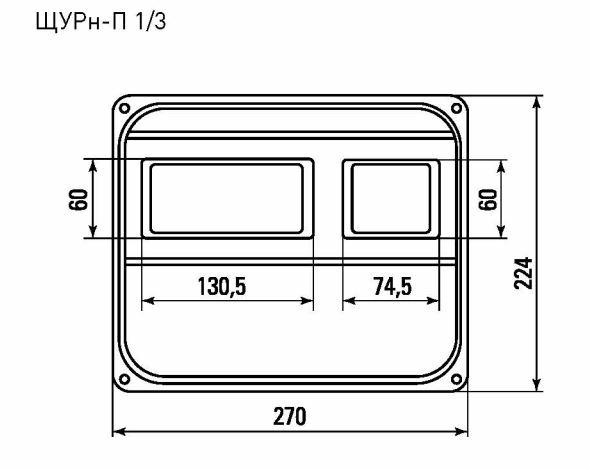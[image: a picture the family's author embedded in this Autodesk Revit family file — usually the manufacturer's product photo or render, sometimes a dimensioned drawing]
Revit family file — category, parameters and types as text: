
# Revit family: EKF_EE_ЩУР_Для_УЭРМС_(580х300х150)_IP31_Basic
name_source: partatom
category: Электрооборудование
units: mm (PartAtom-declared; Revit-internal decimal feet)

## family parameters
Всегда вертикально = Да
На основе рабочей плоскости = Нет
Общий = Нет
При загрузке вырезать с полостями = Нет
Размер круглого соединителя = Использовать диаметр
Тип детали = Силовой щит
Точка расчета площади = Да

## types (1)
- Щит учетно-распред. ЩУР для УЭРМС (580х300х150) IP31 EKF Basic
    ADSK_Единица измерения = компл.
    ADSK_Завод-изготовитель = EKF
    ADSK_Классификация нагрузок = Прочее
    ADSK_Код изделия = uerms-01sh
    ADSK_Количество = 1
    ADSK_Количество фаз = 3
    ADSK_Коэффициент мощности = 1
    ADSK_Марка = ЩУР для УЭРМС IP31
    ADSK_Масса = 0
    ADSK_Материал = RAL 7035_Сталь
    ADSK_Наименование = Щит учетно-распред. ЩУР для УЭРМС (580х300х150) IP31 EKF BasicЩит учетно-распред. ЩУР для УЭРМС (580х300х150) IP31 EKF Basic
    ADSK_Напряжение = 400 В
    ADSK_Номинальная мощность = 0 Вт
    ADSK_Обозначение = ЩУР для УЭРМС IP31
    ADSK_Полная мощность = 0 В·А
    ADSK_Размер_Высота = 580 мм
    ADSK_Размер_Глубина = 150 мм
    ADSK_Размер_Ширина = 300 мм
    ADSK_Ток = 125 А
    Изготовитель = EKF
    Количество DIN-реек = 1
    Количество модулей на DIN-рейке = 12
    Максимальное количество модулей = 12
    Описание = Щит учетно-распред. ЩУР для УЭРМС (580х300х150) IP31 EKF BasicЩит учетно-распред. ЩУР для УЭРМС (580х300х150) IP31 EKF Basic
    Серия номенклатуры = Basic
    Степень защиты IP = IP31
    ТВ = EKF
    Тип = 220 мм
    Тип установки = Навесной
